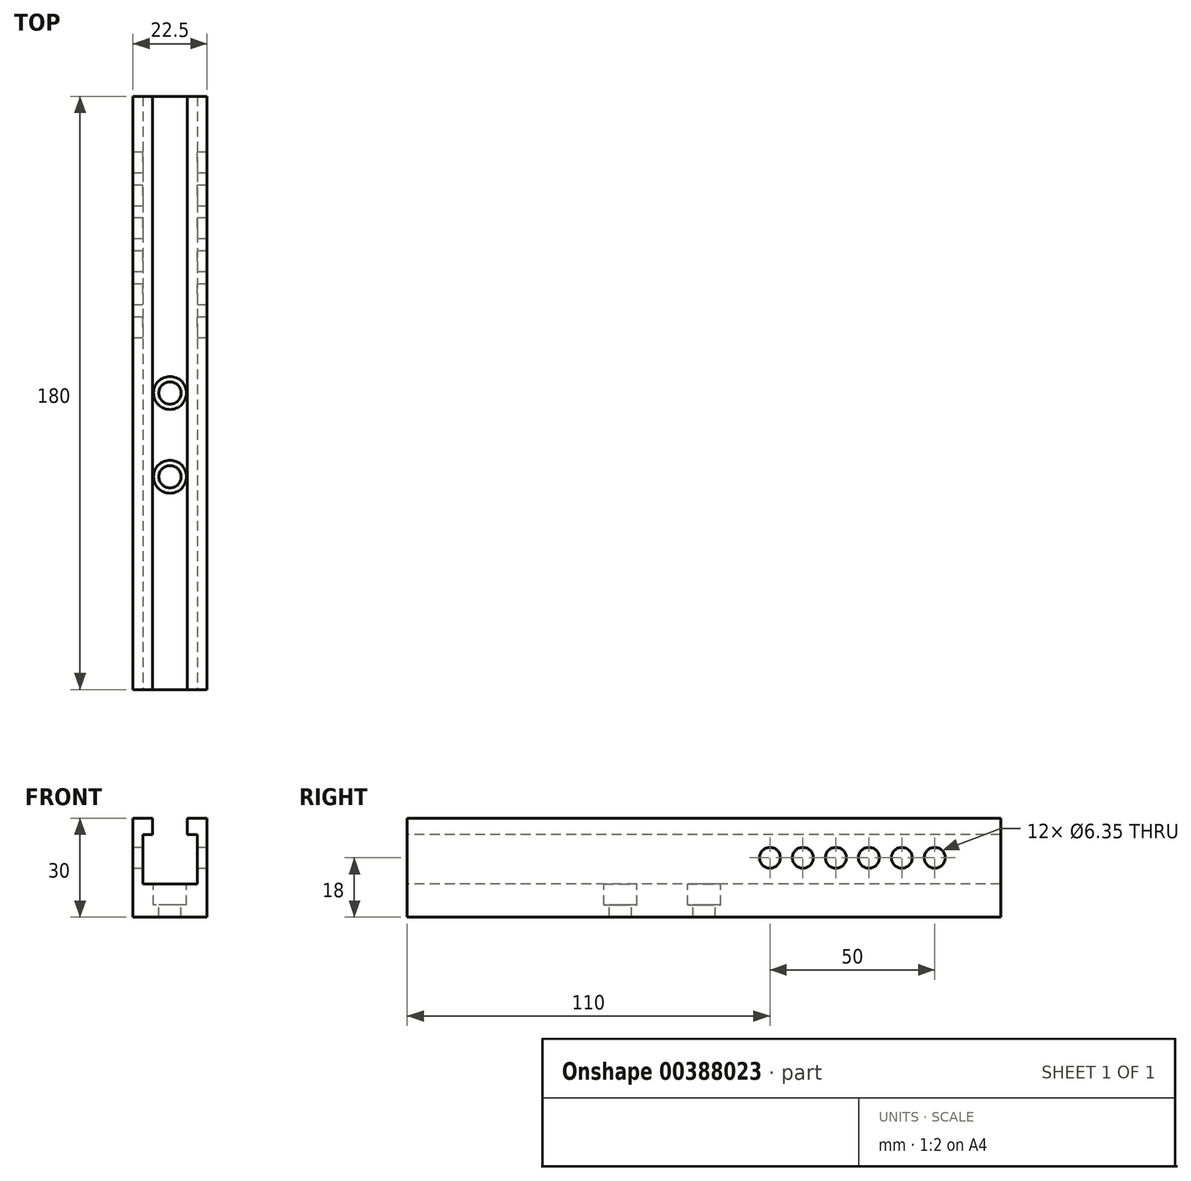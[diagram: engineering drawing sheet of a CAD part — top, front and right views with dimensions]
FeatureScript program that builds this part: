
annotation { "Feature Type Name" : "Feature", "Feature Type Description" : "" }
export const myFeature = defineFeature(function(context is Context, id is Id, definition is map)
    precondition{}
    {
        {
            var Q0;
            Q0=qCreatedBy(makeId("Front.planeOp"),FACE);
            var sketch = newSketch(context, id + "F0", { "sketchPlane" : qUnion([Q0])});
            skLineSegment(sketch, "E0", {"start": v(0, -10) * mm, "end": v(11.25, -10) * mm});
            skLineSegment(sketch, "E1", {"start": v(11.25, -10) * mm, "end": v(11.25, 20) * mm});
            skLineSegment(sketch, "E2", {"start": v(11.25, 20) * mm, "end": v(5.25, 20) * mm});
            skLineSegment(sketch, "E3", {"start": v(5.25, 20) * mm, "end": v(5.25, 0) * mm});
            skLineSegment(sketch, "E4", {"start": v(5.25, 0) * mm, "end": v(0, 0) * mm});
            skLineSegment(sketch, "E5.MirrorCS", {"start": v(-11.25, 20) * mm, "end": v(-5.25, 20) * mm});
            skLineSegment(sketch, "E6.MirrorCS", {"start": v(-5.25, 20) * mm, "end": v(-5.25, 0) * mm});
            skLineSegment(sketch, "E7.MirrorCS", {"start": v(-11.25, -10) * mm, "end": v(-11.25, 20) * mm});
            skLineSegment(sketch, "E8.MirrorCS", {"start": v(0, -10) * mm, "end": v(-11.25, -10) * mm});
            skLineSegment(sketch, "E9.MirrorCS", {"start": v(-5.25, 0) * mm, "end": v(0, 0) * mm});
            skLineSegment(sketch, "E10.bottom", {"start": v(5.25, 15) * mm, "end": v(8.25, 15) * mm});
            skLineSegment(sketch, "E10.top", {"start": v(5.25, 0) * mm, "end": v(8.25, 0) * mm});
            skLineSegment(sketch, "E10.left", {"start": v(5.25, 15) * mm, "end": v(5.25, 0) * mm});
            skLineSegment(sketch, "E10.right", {"start": v(8.25, 15) * mm, "end": v(8.25, 0) * mm});
            skPoint(sketch, "E11.oppositeSnap0", {"position": v(6.75, 0) * mm});
            skLineSegment(sketch, "E11.bottom", {"start": v(-5.25, 15) * mm, "end": v(-8.25, 15) * mm});
            skLineSegment(sketch, "E11.top", {"start": v(-5.25, 0) * mm, "end": v(-8.25, 0) * mm});
            skLineSegment(sketch, "E11.left", {"start": v(-5.25, 15) * mm, "end": v(-5.25, 0) * mm});
            skLineSegment(sketch, "E11.right", {"start": v(-8.25, 15) * mm, "end": v(-8.25, 0) * mm});
            skSolve(sketch);
        }
        {
            var Q0;
            Q0=makeQuery(id+"F0.imprint","IMPRINT",FACE,{"disambiguationData":[TD([[makeQuery(id+"F0.imprint","IMPRINT",EDGE,{"derivedFrom":sQuery(id+"F0.wireOp",EDGE,"E0")}),1.0]])]});
            extrude(context, id + "F1", {"entities" : qUnion([Q0]), "endBound" : BoundingType.SYMMETRIC, "oppositeDirection" : true, "depth" : 180 * mm});
        }
        {
            var Q0;
            Q0=makeQuery(id+"FvRHNmcW906C33A_1.boolean.opBoolean","MERGE",FACE,{"derivedFrom":[makeQuery(id+"F1.opExtrude","SWEPT_FACE",FACE,{"disambiguationData":[OSD([sQuery(id+"F0.wireOp",EDGE,"E4"),sQuery(id+"F0.wireOp",EDGE,"E9.MirrorCS")])]}),makeQuery(id+"FvRHNmcW906C33A_1.opExtrude","SWEPT_FACE",FACE,{"disambiguationData":[OSD([sQuery(id+"FqC0kxr00k9rgX8_1.wireOp",EDGE,"M5M0qwE0-KL02-J3hs-QNf2-4kRAgUoUdY2P")])]})]});
            var sketch = newSketch(context, id + "F2", { "sketchPlane" : qUnion([Q0])});
            skPoint(sketch, "E12", {"position": v(0, 0) * mm});
            skSolve(sketch);
        }
        {
            var Q0;
            Q0=sQuery(id+"F2.wireOp",VERTEX,"E12");
            var Q1;
            Q1=makeQuery(id+"F1.opExtrude","SWEPT_BODY",BODY,{"disambiguationData":[OSD([sQuery(id+"F0.wireOp",EDGE,"E0"),sQuery(id+"F0.wireOp",EDGE,"E1"),sQuery(id+"F0.wireOp",EDGE,"E2"),sQuery(id+"F0.wireOp",EDGE,"E3"),sQuery(id+"F0.wireOp",EDGE,"E4"),sQuery(id+"F0.wireOp",EDGE,"E5.MirrorCS"),sQuery(id+"F0.wireOp",EDGE,"E6.MirrorCS"),sQuery(id+"F0.wireOp",EDGE,"E7.MirrorCS"),sQuery(id+"F0.wireOp",EDGE,"E8.MirrorCS"),sQuery(id+"F0.wireOp",EDGE,"E9.MirrorCS")])]});
            hole(context, id + "F3", {"style" : HoleStyle.C_BORE, "endStyle" : HoleEndStyle.THROUGH, "holeDiameter" : 6.76 * mm, "cBoreDiameter" : 10 * mm, "cBoreDepth" : 6.35 * mm, "isTappedThrough" : true, "tappedDepth" : 12 * mm, "tapClearance" : 3, "locations" : qUnion([Q0]), "scope" : qUnion([Q1])});
        }
        {
            var Q0;
            Q0=makeQuery(id+"F1.opExtrude","SWEPT_FACE",FACE,{"disambiguationData":[OSD([sQuery(id+"F0.wireOp",EDGE,"E1")])]});
            var sketch = newSketch(context, id + "F4", { "sketchPlane" : qUnion([Q0])});
            skCircle(sketch, "E13", {"center": v(20, 8) * mm, "radius": 3.18 * mm});
            skCircle(sketch, "E14", {"center": v(30, 8) * mm, "radius": 3.18 * mm});
            skCircle(sketch, "E15", {"center": v(40, 8) * mm, "radius": 3.18 * mm});
            skCircle(sketch, "E16", {"center": v(50, 8) * mm, "radius": 3.18 * mm});
            skCircle(sketch, "E17", {"center": v(60, 8) * mm, "radius": 3.18 * mm});
            skCircle(sketch, "E18", {"center": v(70, 8) * mm, "radius": 3.18 * mm});
            skLineSegment(sketch, "E19", {"start": v(70, 8) * mm, "end": v(0, 8) * mm, "construction": true});
            skSolve(sketch);
        }
        {
            var Q0;
            Q0=makeQuery(id+"F4.imprint","IMPRINT",FACE,{"disambiguationData":[TD([[makeQuery(id+"F4.imprint","IMPRINT",EDGE,{"derivedFrom":sQuery(id+"F4.wireOp",EDGE,"E15")}),1.0]])]});
            var Q1;
            Q1=makeQuery(id+"F4.imprint","IMPRINT",FACE,{"disambiguationData":[TD([[makeQuery(id+"F4.imprint","IMPRINT",EDGE,{"derivedFrom":sQuery(id+"F4.wireOp",EDGE,"E16")}),1.0]])]});
            var Q2;
            Q2=makeQuery(id+"F4.imprint","IMPRINT",FACE,{"disambiguationData":[TD([[makeQuery(id+"F4.imprint","IMPRINT",EDGE,{"derivedFrom":sQuery(id+"F4.wireOp",EDGE,"E17")}),1.0]])]});
            var Q3;
            Q3=makeQuery(id+"F4.imprint","IMPRINT",FACE,{"disambiguationData":[TD([[makeQuery(id+"F4.imprint","IMPRINT",EDGE,{"derivedFrom":sQuery(id+"F4.wireOp",EDGE,"E14")}),1.0]])]});
            var Q4;
            Q4=makeQuery(id+"F4.imprint","IMPRINT",FACE,{"disambiguationData":[TD([[makeQuery(id+"F4.imprint","IMPRINT",EDGE,{"derivedFrom":sQuery(id+"F4.wireOp",EDGE,"E13")}),1.0]])]});
            var Q5;
            Q5=makeQuery(id+"F4.imprint","IMPRINT",FACE,{"disambiguationData":[TD([[makeQuery(id+"F4.imprint","IMPRINT",EDGE,{"derivedFrom":sQuery(id+"F4.wireOp",EDGE,"E18")}),1.0]])]});
            extrude(context, id + "F5", {"entities" : qUnion([Q0, Q1, Q2, Q3, Q4, Q5]), "operationType" : NewBodyOperationType.REMOVE, "oppositeDirection" : true, "depth" : 25 * mm});
        }
        {
            var Q0;
            Q0=makeQuery(id+"F1.opExtrude","SWEPT_FACE",FACE,{"disambiguationData":[OSD([sQuery(id+"F0.wireOp",EDGE,"E4"),sQuery(id+"F0.wireOp",EDGE,"E9.MirrorCS"),sQuery(id+"F0.wireOp",EDGE,"E10.top"),sQuery(id+"F0.wireOp",EDGE,"E11.top")])]});
            var sketch = newSketch(context, id + "F6", { "sketchPlane" : qUnion([Q0])});
            skPoint(sketch, "E20", {"position": v(0, -25.4) * mm});
            skSolve(sketch);
        }
        {
            var Q0;
            Q0=sQuery(id+"F6.wireOp",VERTEX,"E20");
            var Q1;
            Q1=makeQuery(id+"F1.opExtrude","SWEPT_BODY",BODY,{"disambiguationData":[OSD([sQuery(id+"F0.wireOp",EDGE,"E0"),sQuery(id+"F0.wireOp",EDGE,"E1"),sQuery(id+"F0.wireOp",EDGE,"E2"),sQuery(id+"F0.wireOp",EDGE,"E3"),sQuery(id+"F0.wireOp",EDGE,"E4"),sQuery(id+"F0.wireOp",EDGE,"E5.MirrorCS"),sQuery(id+"F0.wireOp",EDGE,"E6.MirrorCS"),sQuery(id+"F0.wireOp",EDGE,"E7.MirrorCS"),sQuery(id+"F0.wireOp",EDGE,"E8.MirrorCS"),sQuery(id+"F0.wireOp",EDGE,"E9.MirrorCS"),sQuery(id+"F0.wireOp",EDGE,"E10.bottom"),sQuery(id+"F0.wireOp",EDGE,"E10.top"),sQuery(id+"F0.wireOp",EDGE,"E10.right"),sQuery(id+"F0.wireOp",EDGE,"E11.bottom"),sQuery(id+"F0.wireOp",EDGE,"E11.top"),sQuery(id+"F0.wireOp",EDGE,"E11.right")])]});
            hole(context, id + "F7", {"style" : HoleStyle.C_BORE, "endStyle" : HoleEndStyle.THROUGH, "holeDiameter" : 6.76 * mm, "cBoreDiameter" : 10 * mm, "cBoreDepth" : 6.35 * mm, "isTappedThrough" : true, "tappedDepth" : 12 * mm, "tapClearance" : 3, "locations" : qUnion([Q0]), "scope" : qUnion([Q1])});
        }
    });
